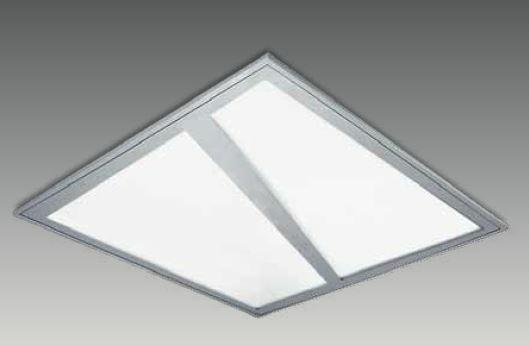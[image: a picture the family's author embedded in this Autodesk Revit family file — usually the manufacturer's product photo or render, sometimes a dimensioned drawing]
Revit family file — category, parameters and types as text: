
# Revit family: G 6060 ORI
name_source: partatom
category: Lighting Fixtures
revit_build: Autodesk Revit 2017 (Build: 20160225_1515(x64)
units: mm (PartAtom-declared; Revit-internal decimal feet)

## family parameters
Always vertical = Yes
Cut with Voids When Loaded = No
Host = Ceiling
Light Source = Yes
OmniClass Number = 23.80.70.11
OmniClass Title = Luminaries for Internal Lighting
Part Type = Normal
Room Calculation Point = No
Round Connector Dimension = Use Diameter
Shared = No

## types (4) — shared parameters
Color Filter = 16777215
Dimming Lamp Color Temperature Shift = <None>
Emit Shape Visible in Rendering = Yes
Emit from Rectangle Length = 570 mm  [stored 1.87008 ft]
Emit from Rectangle Width = 570 mm  [stored 1.87008 ft]
Light Source Symbol Size = 610 mm
Manufacturer = ARLIGHT
Type Image = G 6060 ORI.JPG

## per-type parameters (varying)
| type | Wattage Comments |
| GORI.6060.36.30 | 36 |
| GORI.6060.36.40 | 36 |
| GORI.6060.28.30 | 28 |
| GORI.6060.28.40 | 28 |

note: [stored X ft] marks values corroborated as IEEE doubles in the binary element streams (Revit-internal decimal feet)

## geometry (parser evidence)
native form markers: Sweep x2
no freeform markers — native parametric forms only
